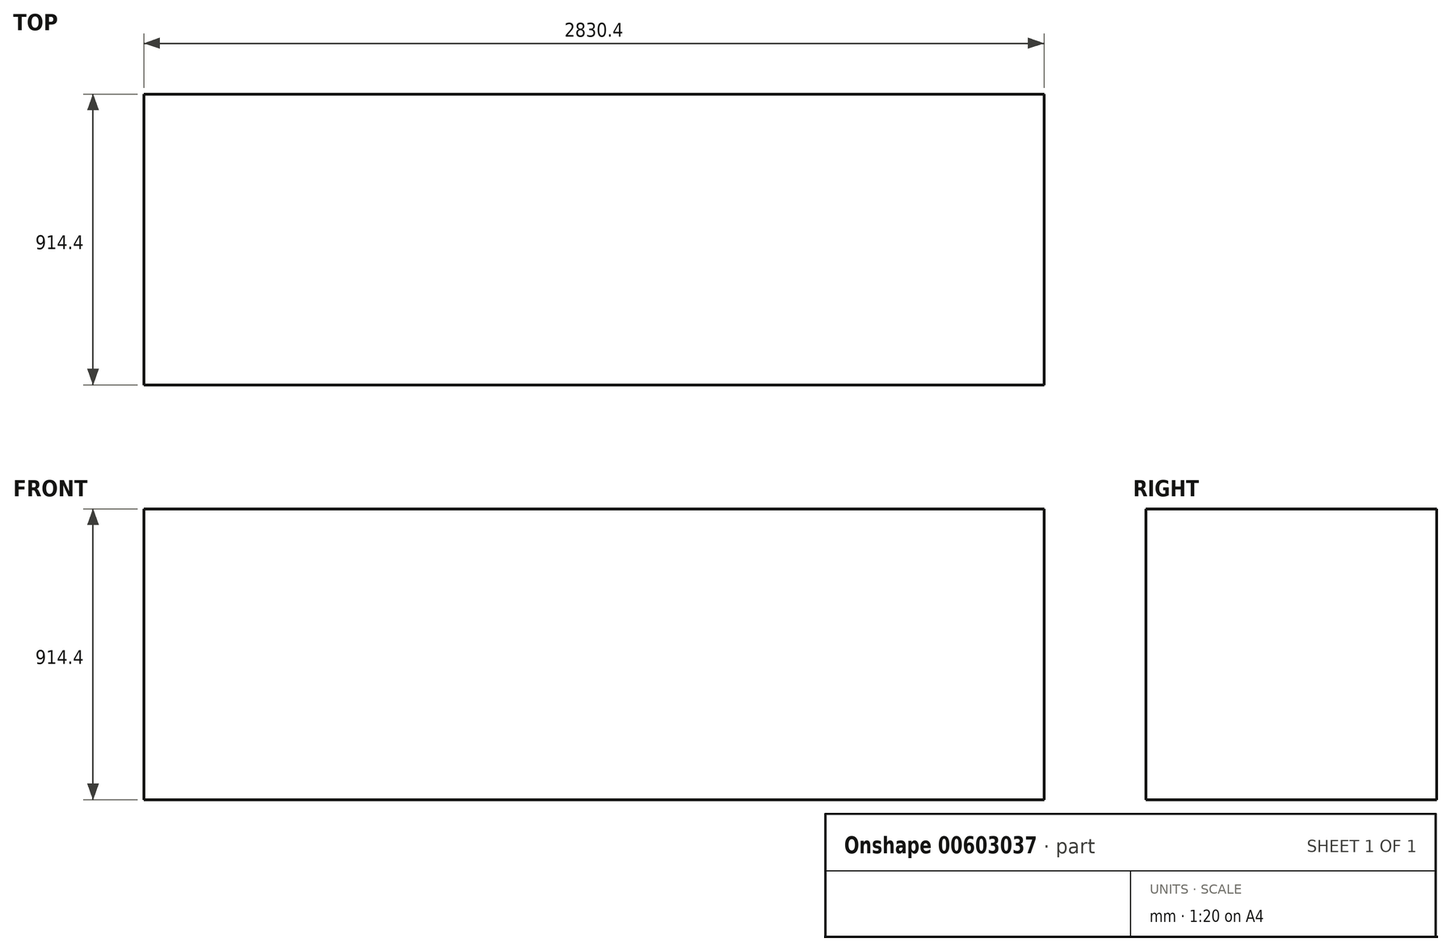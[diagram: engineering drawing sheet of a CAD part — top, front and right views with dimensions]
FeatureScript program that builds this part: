
annotation { "Feature Type Name" : "Feature", "Feature Type Description" : "" }
export const myFeature = defineFeature(function(context is Context, id is Id, definition is map)
    precondition{}
    {
        {
            var Q0;
            Q0=qCreatedBy(makeId("Top.planeOp"),FACE);
            var sketch = newSketch(context, id + "F0", { "sketchPlane" : qUnion([Q0])});
            skLineSegment(sketch, "E0.bottom", {"start": v(-1421.34, 459.97) * mm, "end": v(1409.06, 459.97) * mm});
            skLineSegment(sketch, "E0.top", {"start": v(-1421.34, -454.43) * mm, "end": v(1409.06, -454.43) * mm});
            skLineSegment(sketch, "E0.left", {"start": v(-1421.34, 459.97) * mm, "end": v(-1421.34, -454.43) * mm});
            skLineSegment(sketch, "E0.right", {"start": v(1409.06, 459.97) * mm, "end": v(1409.06, -454.43) * mm});
            skSolve(sketch);
        }
        {
            var Q0;
            Q0 = qSketchRegion(id + "F0", true);
            extrude(context, id + "F1", {"entities" : qUnion([Q0]), "depth" : 914.4 * mm, "offsetDistance" : 25.4 * mm});
        }
    });
